# Revit family: Sound_Silencer_222
name_source: partatom
category: Generic Models
units: mm (PartAtom-declared; Revit-internal decimal feet)

## family parameters
Can host rebar = No
Classification Number = 23.35.70.11.14.11
Cut with Voids When Loaded = No
Host = Face
Maintain Annotation Orientation = No
Part Type = Normal
Room Calculation Point = No
Round Connector Dimension = Use Diameter
Shared = No

## types (2) — shared parameters
Assembly Code = F1030100
Dba Acoustical Panel = PEPP Panel
Default Elevation = 4' - 0"
Keynote = 09800
Manufacturer = Acoustical Surfaces Inc.
Porous Expanded Polypropyene = PEPP Panel White
zero-valued in all types: Expected Lifespan (Years), Maintenance Schedule (Months), Warranty Duration (Years)

## per-type parameters (varying)
| type | Description | Model | Type Comments | URL |
| DBA Acoustical Panel |  |  |  |  |
| Sound Silencer | Acoustical Panel | Sound Silencer | Porous Expanded Polypropylene | www.acousticalsurfaces.com |

## geometry (parser evidence)
native form markers: Sweep x1
no freeform markers — native parametric forms only
